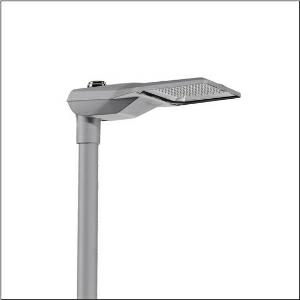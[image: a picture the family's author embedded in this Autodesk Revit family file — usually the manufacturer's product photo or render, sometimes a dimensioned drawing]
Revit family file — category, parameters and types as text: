
# Revit family: streetlight_sl_21_midi___stw1_0a_5xe7e47n08lb_5353
name_source: partatom
category: Lighting Fixtures
units: mm (PartAtom-declared; Revit-internal decimal feet)

## family parameters
Cut with Voids When Loaded = No
Host = Face
Light Source = No
Part Type = Normal
Room Calculation Point = No
Round Connector Dimension = Use Diameter
Shared = No

## types (1)
- --- (1 x LED, 14950 lm, 98.3 W, 4000K)
    Apparent Load = 98 VA
    CIE Flux Codes = 38 75 98 100 100
    Color Rendering = 70
    Color Temperature = 4000K
    Default Elevation = 1800 mm
    Description = Streetlight SL 21 midi, mast luminaire, primary light control with lens, of PMMA, primary optical cover: cover, of toughened safety glass, transparent, light distribution: STW1.0a, light emission: direct distribution, primary light characteristic: asymmetric, installation type: side-entry, LED, 3G 2.5mm², High Power LED, rated luminous flux: 14.950lm, luminous efficacy: 152lm/W, light colour: 740, colour temperature: 4000K, control gear: NEMA (7pin), control: overheat protection, pre-setting: linear dimming characteristic, constant luminous flux control, time-dependent luminous flux control, flexible luminous flux parameterisation, mains connection: 220..240V, AC, 50/60Hz, connection cable pre-assembled, cable length: 10,5m, wiring characteristics: H05VV-F, start of lifetime: 98W, end of service life: 101W, reduction: 45W, luminaire housing, of diecast aluminium (EN AC-44300), powder-coated, Siteco® metallic grey (DB 702S), corrosivity category C5 mid according to DIN EN ISO 12944, multi-level sealing system, sealing non-destructively replaceable, inclination adjustable: 0°, 5°, 10°, 15°, length: 644mm, width: 335mm, height: 110mm, spigot size: 42mm (side-entry), mounting height: 4..8m, protection rating (complete): IP66, insulation class (complete): insulation class I (protective earthing), certification: CE, ENEC, ENEC+, VDE, impact resistance: IK10, permissible operating ambient temperature for outdoor applications: -40..+50°C, standard-compliant lighting for roads and squares, packaging unit: 1 piece

Light Distribution: STW1.0a
    Height = 111 mm
    Lamp = 1 x LED
    Lamp Light Flux = 14950 lm
    Lamp Power = 98.3 W
    Lamp count = 1
    Length = 644 mm
    Luminous efficacy = 152 lm/W
    Manufacturer = Siteco
    ModVariant = No
    Model = 5XE7E47N08LB
    Number of Poles = 1
    OnlyDefault = Yes
    Power Factor = 1
    Product Name = Streetlight SL 21 midi | STW1.0a
    Product group = mast luminaire | pylon top
    ProductGroupID = 6100
    Protection Class = Protection class I
    Protection Degree = IP 66
    RLX_Detail_Level = 1
    RLX_Emergency_Light_Flux = 0 lm
    RLX_Emergency_Type = 0
    RLX_Emergency_Type_DB = No
    RlxData = <blob elided: 26713 chars, md5=08064f8d>
    Socket = socket
    Standby Power = 0 W
    System Light Flux = 14950 lm
    System Power = 98 W
    Type Comments = factory setting: luminous flux: 100 % | dim-lin: 254 | 1020 mA
    Type Image = l_1294377.jpg
    URL = http://relux.com
    VarID = @adj_156959
    Voltage = 0 V
    Weight = 0.00 kg
    Width = 336 mm

## geometry (parser evidence)
native form markers: Blend x4, Sweep x9
no freeform markers — native parametric forms only
